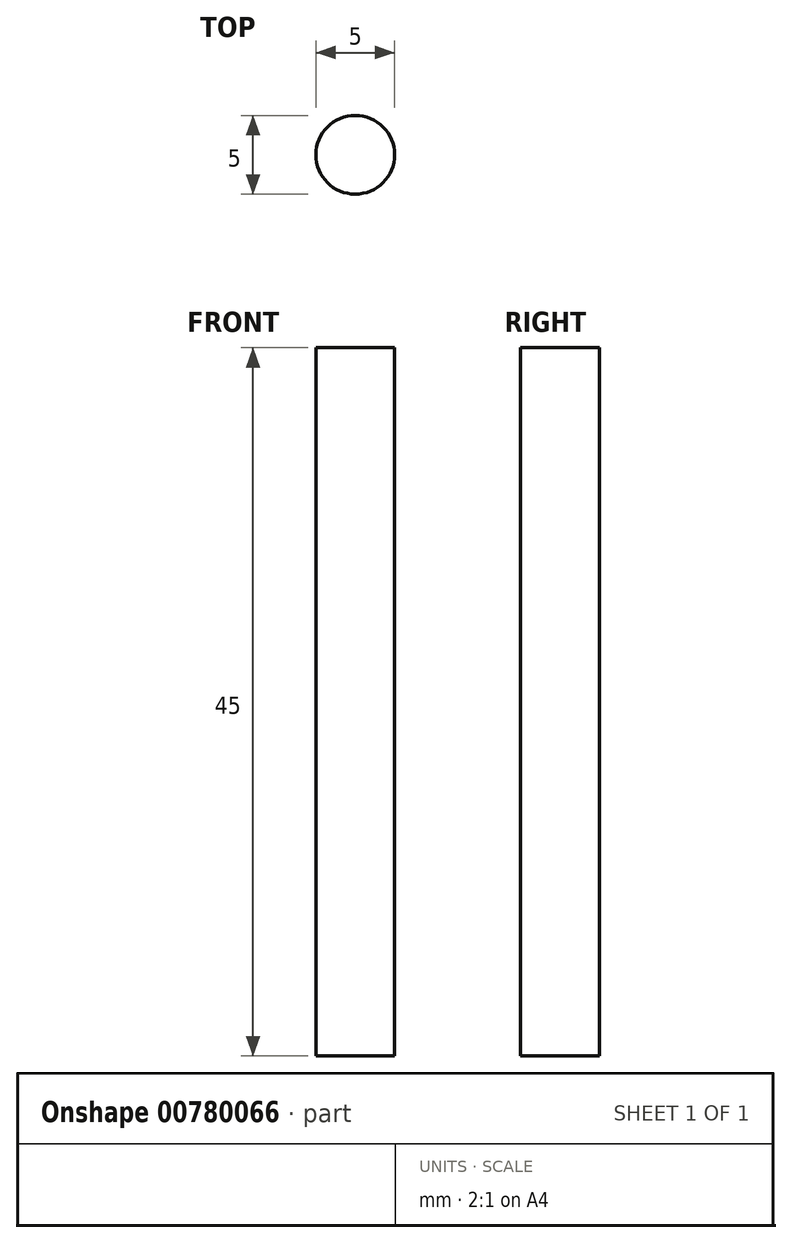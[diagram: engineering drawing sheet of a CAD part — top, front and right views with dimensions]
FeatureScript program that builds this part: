
annotation { "Feature Type Name" : "Feature", "Feature Type Description" : "" }
export const myFeature = defineFeature(function(context is Context, id is Id, definition is map)
    precondition{}
    {
        {
            var Q0;
            Q0=qCreatedBy(makeId("Top.planeOp"),FACE);
            var sketch = newSketch(context, id + "F0", { "sketchPlane" : qUnion([Q0])});
            skCircle(sketch, "E0", {"center": v(0, 0) * mm, "radius": 2.5 * mm});
            skSolve(sketch);
        }
        {
            var Q0;
            Q0 = qSketchRegion(id + "F0", true);
            extrude(context, id + "F1", {"entities" : qUnion([Q0]), "depth" : 45 * mm, "offsetDistance" : 25 * mm});
        }
    });
